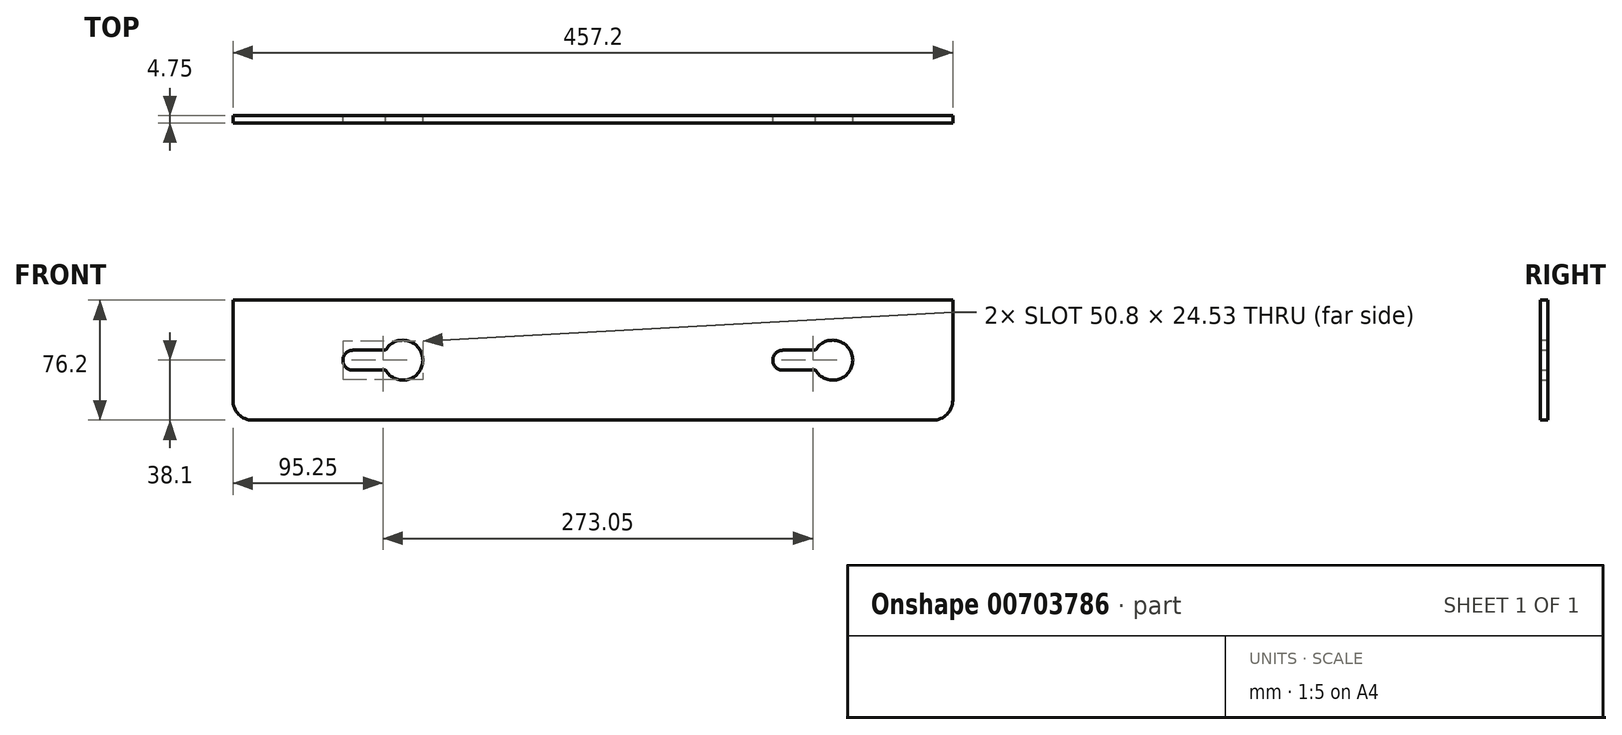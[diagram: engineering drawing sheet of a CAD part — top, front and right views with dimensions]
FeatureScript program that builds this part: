
annotation { "Feature Type Name" : "Feature", "Feature Type Description" : "" }
export const myFeature = defineFeature(function(context is Context, id is Id, definition is map)
    precondition{}
    {
        {
            var Q0;
            Q0=qCreatedBy(makeId("Front.planeOp"),FACE);
            var sketch = newSketch(context, id + "F0", { "sketchPlane" : qUnion([Q0])});
            skLineSegment(sketch, "E0", {"start": v(304.8, -304.8) * mm, "end": v(0, -304.8) * mm});
            skLineSegment(sketch, "E1", {"start": v(0, -304.8) * mm, "end": v(-152.4, -304.8) * mm});
            skLineSegment(sketch, "E2", {"start": v(-152.4, -304.8) * mm, "end": v(-152.4, -368.3) * mm});
            skLineSegment(sketch, "E3", {"start": v(-139.7, -381) * mm, "end": v(292.1, -381) * mm});
            skLineSegment(sketch, "E4", {"start": v(304.8, -368.3) * mm, "end": v(304.8, -304.8) * mm});
            skArc(sketch, "E5", {"start": v(-55.45, -349.25) * mm, "mid": v(-31.75, -342.9) * mm, "end": v(-55.45, -336.55) * mm});
            skPoint(sketch, "E5.centerSnap0", {"position": v(-152.4, -342.9) * mm});
            skArc(sketch, "E6", {"start": v(217.6, -349.25) * mm, "mid": v(241.3, -342.9) * mm, "end": v(217.6, -336.55) * mm});
            skPoint(sketch, "E6.centerSnap0", {"position": v(304.8, -342.9) * mm});
            skArc(sketch, "E7", {"start": v(-76.2, -336.55) * mm, "mid": v(-82.55, -342.9) * mm, "end": v(-76.2, -349.25) * mm});
            skArc(sketch, "E8", {"start": v(196.85, -336.55) * mm, "mid": v(190.5, -342.9) * mm, "end": v(196.85, -349.25) * mm});
            skLineSegment(sketch, "E9", {"start": v(196.85, -336.55) * mm, "end": v(217.6, -336.55) * mm});
            skLineSegment(sketch, "E10", {"start": v(196.85, -349.25) * mm, "end": v(217.6, -349.25) * mm});
            skLineSegment(sketch, "E11", {"start": v(-76.2, -336.55) * mm, "end": v(-55.45, -336.55) * mm});
            skLineSegment(sketch, "E12", {"start": v(-76.2, -349.25) * mm, "end": v(-55.45, -349.25) * mm});
            skPoint(sketch, "E13.visualSharp", {"position": v(-152.4, -381) * mm});
            skArc(sketch, "E13.filletArc", {"start": v(-152.4, -368.3) * mm, "mid": v(-148.68, -377.28) * mm, "end": v(-139.7, -381) * mm});
            skPoint(sketch, "E14.visualSharp", {"position": v(-76.2, -228.6) * mm});
            skPoint(sketch, "E15.visualSharp", {"position": v(304.8, -381) * mm});
            skArc(sketch, "E15.filletArc", {"start": v(292.1, -381) * mm, "mid": v(301.08, -377.28) * mm, "end": v(304.8, -368.3) * mm});
            skPoint(sketch, "E16.visualSharp", {"position": v(228.6, -228.6) * mm});
            skPoint(sketch, "E17.start.orphan", {"position": v(-152.4, 355.6) * mm});
            skPoint(sketch, "E18.start.orphan", {"position": v(304.8, 0) * mm});
            skSolve(sketch);
        }
        {
            var Q0;
            Q0=makeQuery(id+"F0.imprint","IMPRINT",FACE,{"disambiguationData":[TD([[makeQuery(id+"F0.imprint","IMPRINT",EDGE,{"derivedFrom":sQuery(id+"F0.wireOp",EDGE,"501b2094-21bc-4b17-b7b0-be7431d77841")}),1.0]])]});
            var Q1;
            Q1=makeQuery(id+"F0.imprint","IMPRINT",FACE,{"disambiguationData":[TD([[makeQuery(id+"F0.imprint","IMPRINT",EDGE,{"derivedFrom":sQuery(id+"F0.wireOp",EDGE,"E0")}),1.0]])]});
            extrude(context, id + "F1", {"entities" : qUnion([Q0, Q1]), "depth" : 4.75 * mm, "offsetDistance" : 25.4 * mm});
        }
    });
